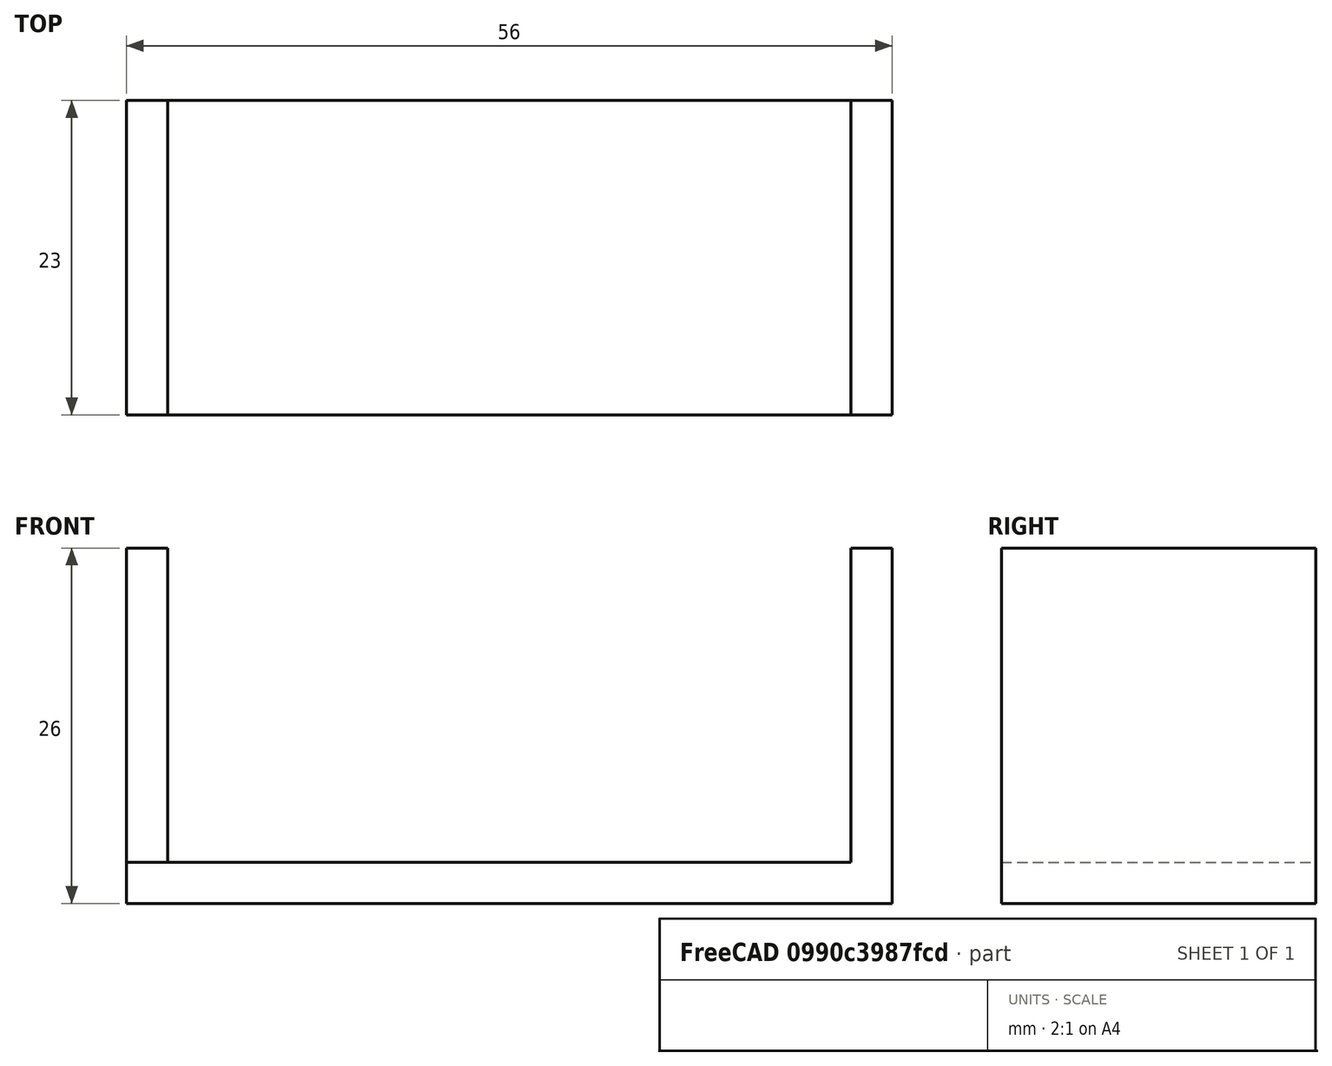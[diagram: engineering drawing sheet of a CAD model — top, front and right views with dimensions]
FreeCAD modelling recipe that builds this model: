
FCSTD DOCUMENT  (FreeCAD 0.19R24366 (Git))
Label: servoHolderForLaptop
License: All rights reserved
LicenseURL: http://en.wikipedia.org/wiki/All_rights_reserved
objects: Part::Box×2, Part::FeaturePython×1, Part::Fuse×1
note: 3 computed .brp shape members not serialized (recipe doc carries the construction recipe); baked Part::Feature solids carry a one-line shape summary decoded from their .brp

FEATURE [Part::Box] Box  label="base"
  AttacherType = Attacher::AttachEngine3D
  Height = 23
  Length = 3
  Placement = pos=(0,0,3) rot=(0,0,1;0rad)
  Width = 23
FEATURE [Part::Box] Box001  label="wall"
  AttacherType = Attacher::AttachEngine3D
  Height = 3
  Length = 56
  Width = 23
FEATURE [Part::FeaturePython] Array  label="baseAndTopArray"  # Draft array (typed FeaturePython)
  Angle = 360
  ArrayType = 0
  Axis = (0,0,1)
  Base = -> Box
  Center = (0,0,0)
  Count = 2
  ExpandArray = false
  Fuse = false
  IntervalAxis = (0,0,0)
  IntervalX = (53,0,0)
  IntervalY = (0,0,0)
  IntervalZ = (0,0,0)
  NumberCircles = 3
  NumberPolar = 5
  NumberX = 2
  NumberY = 1
  NumberZ = 1
  PlacementList = 2 placements: [(0,0,3),(53,0,3)]
  RadialDistance = 50
  ScaleList = (2) [(1,1,1),(1,1,1)]
  Symmetry = 1
  TangentialDistance = 25
FEATURE [Part::Fuse] Fusion  label="servoHolderForLaptop"
  Base = -> Box001
  Tool = -> Array
